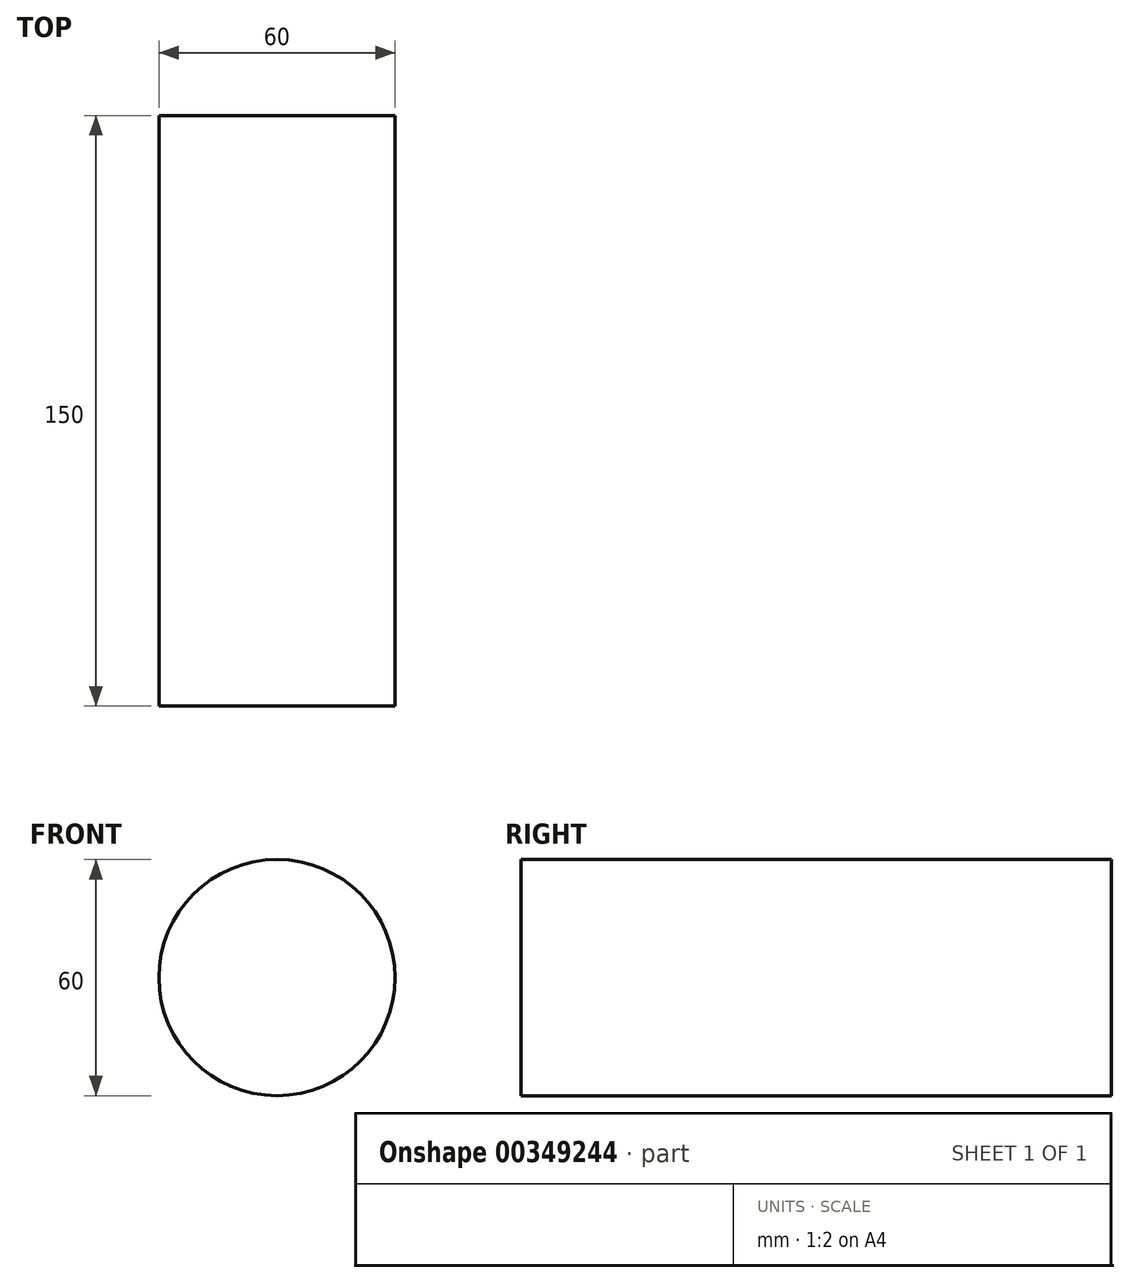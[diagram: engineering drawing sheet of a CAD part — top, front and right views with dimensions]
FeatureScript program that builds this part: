
annotation { "Feature Type Name" : "Feature", "Feature Type Description" : "" }
export const myFeature = defineFeature(function(context is Context, id is Id, definition is map)
    precondition{}
    {
        {
            var Q0;
            Q0=qCreatedBy(makeId("Front.planeOp"),FACE);
            var sketch = newSketch(context, id + "F0", { "sketchPlane" : qUnion([Q0])});
            skCircle(sketch, "E0", {"center": v(0, 0) * mm, "radius": 30 * mm});
            skSolve(sketch);
        }
        {
            var Q0;
            Q0 = qSketchRegion(id + "F0", true);
            extrude(context, id + "F1", {"entities" : qUnion([Q0]), "depth" : 150 * mm});
        }
    });
